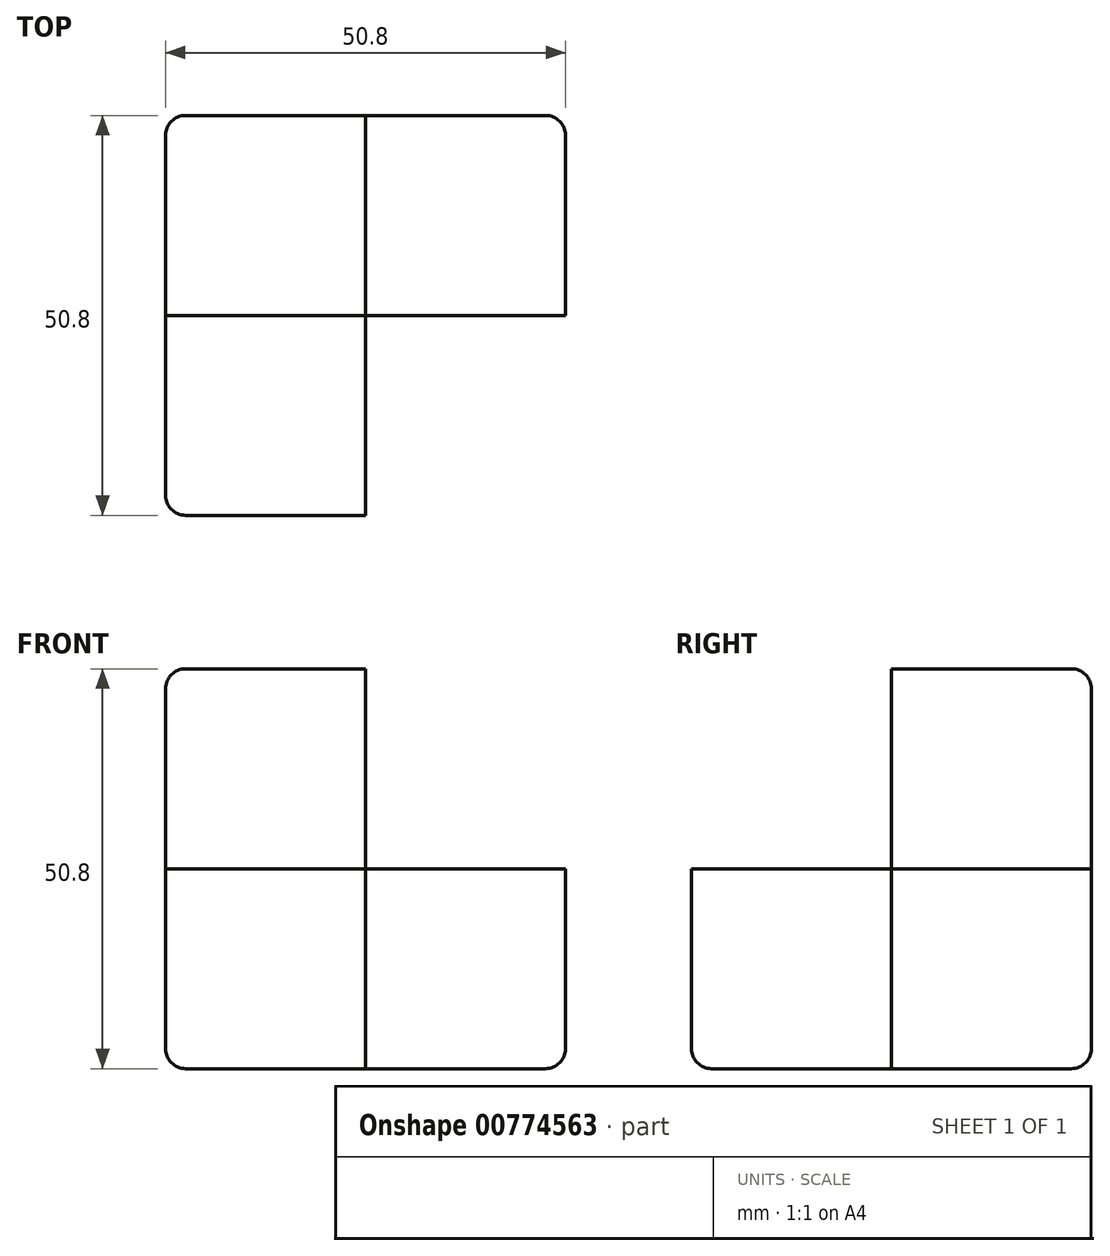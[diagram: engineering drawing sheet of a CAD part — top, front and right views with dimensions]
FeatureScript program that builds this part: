
annotation { "Feature Type Name" : "Feature", "Feature Type Description" : "" }
export const myFeature = defineFeature(function(context is Context, id is Id, definition is map)
    precondition{}
    {
        {
            var Q0;
            Q0=qCreatedBy(makeId("Front.planeOp"),FACE);
            var sketch = newSketch(context, id + "F0", { "sketchPlane" : qUnion([Q0])});
            skLineSegment(sketch, "E0.bottom", {"start": v(0, 0) * mm, "end": v(50.8, 0) * mm});
            skLineSegment(sketch, "E0.top", {"start": v(0, 50.8) * mm, "end": v(50.8, 50.8) * mm});
            skLineSegment(sketch, "E0.left", {"start": v(0, 0) * mm, "end": v(0, 50.8) * mm});
            skLineSegment(sketch, "E0.right", {"start": v(50.8, 0) * mm, "end": v(50.8, 50.8) * mm});
            skSolve(sketch);
        }
        {
            var Q0;
            Q0=makeQuery(id+"F0.imprint","IMPRINT",FACE,{"disambiguationData":[TD([[makeQuery(id+"F0.imprint","IMPRINT",EDGE,{"derivedFrom":sQuery(id+"F0.wireOp",EDGE,"E0.bottom")}),1.0]])]});
            extrude(context, id + "F1", {"entities" : qUnion([Q0]), "depth" : 50.8 * mm, "offsetDistance" : 25.4 * mm});
        }
        {
            var Q0;
            Q0=makeQuery(id+"F1.opExtrude","SWEPT_FACE",FACE,{"disambiguationData":[OSD([sQuery(id+"F0.wireOp",EDGE,"E0.top")])]});
            var sketch = newSketch(context, id + "F2", { "sketchPlane" : qUnion([Q0])});
            skLineSegment(sketch, "E1.bottom", {"start": v(0, 0) * mm, "end": v(25.4, 0) * mm});
            skLineSegment(sketch, "E1.top", {"start": v(0, -25.4) * mm, "end": v(25.4, -25.4) * mm});
            skLineSegment(sketch, "E1.left", {"start": v(0, 0) * mm, "end": v(0, -25.4) * mm});
            skLineSegment(sketch, "E1.right", {"start": v(25.4, 0) * mm, "end": v(25.4, -25.4) * mm});
            skSolve(sketch);
        }
        {
            var Q0;
            {var subQ4=sQuery(id+"F2.wireOp",EDGE,"E1.top");Q0=makeQuery(id+"F2.imprint","IMPRINT",FACE,{"disambiguationData":[TD([[makeQuery(id+"F2.imprint","IMPRINT",EDGE,{"derivedFrom":subQ4}),-1.0]])]});}
            extrude(context, id + "F3", {"entities" : qUnion([Q0]), "operationType" : NewBodyOperationType.REMOVE, "oppositeDirection" : true, "depth" : 25.4 * mm, "offsetDistance" : 25.4 * mm});
        }
        {
            var Q0;
            Q0=makeQuery(id+"F3.boolean.opBoolean","COPY",FACE,{"derivedFrom":makeQuery(id+"F3.opExtrude","CAP_FACE",FACE,{"disambiguationData":[OSD([sQuery(id+"F0.wireOp",EDGE,"E0.top"),sQuery(id+"F0.wireOp",EDGE,"E0.left"),sQuery(id+"F0.wireOp",EDGE,"E0.right"),sQuery(id+"F2.wireOp",EDGE,"E1.top"),sQuery(id+"F2.wireOp",EDGE,"E1.right")])],"isStart":false})});
            var sketch = newSketch(context, id + "F4", { "sketchPlane" : qUnion([Q0])});
            skLineSegment(sketch, "E2.bottom", {"start": v(50.8, -50.8) * mm, "end": v(25.4, -50.8) * mm});
            skLineSegment(sketch, "E2.top", {"start": v(50.8, -25.4) * mm, "end": v(25.4, -25.4) * mm});
            skLineSegment(sketch, "E2.left", {"start": v(50.8, -50.8) * mm, "end": v(50.8, -25.4) * mm});
            skLineSegment(sketch, "E2.right", {"start": v(25.4, -50.8) * mm, "end": v(25.4, -25.4) * mm});
            skSolve(sketch);
        }
        {
            var Q0;
            Q0=makeQuery(id+"F4.imprint","IMPRINT",FACE,{"disambiguationData":[TD([[makeQuery(id+"F4.imprint","IMPRINT",EDGE,{"derivedFrom":sQuery(id+"F4.wireOp",EDGE,"E2.bottom")}),1.0]])]});
            extrude(context, id + "F5", {"entities" : qUnion([Q0]), "operationType" : NewBodyOperationType.REMOVE, "oppositeDirection" : true, "depth" : 25.4 * mm, "offsetDistance" : 25.4 * mm});
        }
        {
            var Q0;
            Q0=makeQuery(id+"F3.boolean.opBoolean","COPY",EDGE,{"derivedFrom":makeQuery(id+"F3.opExtrude","CAP_EDGE",EDGE,{"disambiguationData":[OSD([sQuery(id+"F0.wireOp",EDGE,"E0.top"),sQuery(id+"F0.wireOp",EDGE,"E0.right")])],"isStart":false})});
            var Q1;
            Q1=makeQuery(id+"F3.boolean.opBoolean","COPY",EDGE,{"derivedFrom":makeQuery(id+"F3.opExtrude","CAP_EDGE",EDGE,{"disambiguationData":[OSD([sQuery(id+"F0.wireOp",EDGE,"E0.top"),sQuery(id+"F0.wireOp",EDGE,"E0.left")])],"isStart":false})});
            var Q2;
            Q2=makeQuery(id+"F3.boolean.opBoolean","COPY",EDGE,{"derivedFrom":makeQuery(id+"F3.opExtrude","CAP_EDGE",EDGE,{"disambiguationData":[OSD([sQuery(id+"F2.wireOp",EDGE,"E1.right")])],"isStart":true})});
            var Q3;
            Q3=makeQuery(id+"F3.boolean.opBoolean","COPY",EDGE,{"derivedFrom":makeQuery(id+"F3.opExtrude","CAP_EDGE",EDGE,{"disambiguationData":[OSD([sQuery(id+"F2.wireOp",EDGE,"E1.top")])],"isStart":true})});
            var Q4;
            Q4=makeQuery(id+"F1.opExtrude","SWEPT_EDGE",EDGE,{"disambiguationData":[OSD([sQuery(id+"F0.wireOp",EDGE,"E0.top"),sQuery(id+"F0.wireOp",EDGE,"E0.left")])]});
            var Q5;
            Q5=makeQuery(id+"F1.opExtrude","CAP_EDGE",EDGE,{"disambiguationData":[OSD([sQuery(id+"F0.wireOp",EDGE,"E0.top")])],"isStart":true});
            var Q6;
            {var subQ0=sQuery(id+"F0.wireOp",EDGE,"E0.top");var subQ1=makeQuery(id+"F1.opExtrude","CAP_EDGE",EDGE,{"disambiguationData":[OSD([subQ0])],"isStart":true});Q6=makeQuery(id+"F3.boolean.opBoolean","COPY",EDGE,{"derivedFrom":makeQuery(id+"F3.opExtrude","CAP_EDGE",EDGE,{"disambiguationData":[OSD([subQ0]),TDD([makeQuery(id+"F2.imprint","IMPRINT",EDGE,{"disambiguationData":[TD([[makeQuery(id+"F2.imprint","INTERSECT",VERTEX,{"derivedFrom":[makeQuery(id+"F1.opExtrude","SWEPT_EDGE",EDGE,{"disambiguationData":[OSD([subQ0,sQuery(id+"F0.wireOp",EDGE,"E0.right")])]}),subQ1]}),1.0]])],"derivedFrom":subQ1})])],"isStart":false})});}
            var Q7;
            Q7=makeQuery(id+"F3.boolean.opBoolean","COPY",EDGE,{"derivedFrom":makeQuery(id+"F3.opExtrude","SWEPT_EDGE",EDGE,{"disambiguationData":[OSD([sQuery(id+"F0.wireOp",EDGE,"E0.top"),sQuery(id+"F2.wireOp",EDGE,"E1.bottom"),sQuery(id+"F2.wireOp",EDGE,"E1.right")])]})});
            var Q8;
            {var subQ0=sQuery(id+"F0.wireOp",EDGE,"E0.top");Q8=makeQuery(id+"F3.boolean.opBoolean","COPY",EDGE,{"derivedFrom":makeQuery(id+"F3.opExtrude","CAP_EDGE",EDGE,{"disambiguationData":[OSD([subQ0]),TDD([makeQuery(id+"F2.imprint","IMPRINT",EDGE,{"derivedFrom":makeQuery(id+"F1.opExtrude","CAP_EDGE",EDGE,{"disambiguationData":[OSD([subQ0])],"isStart":false})})])],"isStart":false})});}
            var Q9;
            Q9=makeQuery(id+"F1.opExtrude","CAP_EDGE",EDGE,{"disambiguationData":[OSD([sQuery(id+"F0.wireOp",EDGE,"E0.bottom")])],"isStart":false});
            var Q10;
            Q10=makeQuery(id+"F5.boolean.opBoolean","COPY",EDGE,{"derivedFrom":makeQuery(id+"F5.opExtrude","CAP_EDGE",EDGE,{"disambiguationData":[OSD([sQuery(id+"F4.wireOp",EDGE,"E2.top")])],"isStart":false})});
            var Q11;
            Q11=makeQuery(id+"F5.boolean.opBoolean","COPY",EDGE,{"derivedFrom":makeQuery(id+"F5.opExtrude","SWEPT_EDGE",EDGE,{"disambiguationData":[OSD([sQuery(id+"F0.wireOp",EDGE,"E0.top"),sQuery(id+"F0.wireOp",EDGE,"E0.right"),sQuery(id+"F4.wireOp",EDGE,"E2.top"),sQuery(id+"F4.wireOp",EDGE,"E2.left")])]})});
            var Q12;
            Q12=makeQuery(id+"F5.boolean.opBoolean","COPY",EDGE,{"derivedFrom":makeQuery(id+"F5.opExtrude","SWEPT_EDGE",EDGE,{"disambiguationData":[OSD([sQuery(id+"F0.wireOp",EDGE,"E0.top"),sQuery(id+"F4.wireOp",EDGE,"E2.bottom"),sQuery(id+"F4.wireOp",EDGE,"E2.right")])]})});
            var Q13;
            Q13=makeQuery(id+"F1.opExtrude","CAP_EDGE",EDGE,{"disambiguationData":[OSD([sQuery(id+"F0.wireOp",EDGE,"E0.left")])],"isStart":false});
            var Q14;
            Q14=makeQuery(id+"F1.opExtrude","CAP_EDGE",EDGE,{"disambiguationData":[OSD([sQuery(id+"F0.wireOp",EDGE,"E0.bottom")])],"isStart":true});
            var Q15;
            Q15=makeQuery(id+"F1.opExtrude","SWEPT_EDGE",EDGE,{"disambiguationData":[OSD([sQuery(id+"F0.wireOp",EDGE,"E0.bottom"),sQuery(id+"F0.wireOp",EDGE,"E0.right")])]});
            var Q16;
            Q16=makeQuery(id+"F1.opExtrude","CAP_EDGE",EDGE,{"disambiguationData":[OSD([sQuery(id+"F0.wireOp",EDGE,"E0.left")])],"isStart":true});
            var Q17;
            Q17=makeQuery(id+"F1.opExtrude","SWEPT_EDGE",EDGE,{"disambiguationData":[OSD([sQuery(id+"F0.wireOp",EDGE,"E0.bottom"),sQuery(id+"F0.wireOp",EDGE,"E0.left")])]});
            var Q18;
            Q18=makeQuery(id+"F1.opExtrude","CAP_EDGE",EDGE,{"disambiguationData":[OSD([sQuery(id+"F0.wireOp",EDGE,"E0.right")])],"isStart":true});
            var Q19;
            Q19=makeQuery(id+"F3.boolean.opBoolean","COPY",EDGE,{"derivedFrom":makeQuery(id+"F3.opExtrude","SWEPT_EDGE",EDGE,{"disambiguationData":[OSD([sQuery(id+"F0.wireOp",EDGE,"E0.top"),sQuery(id+"F0.wireOp",EDGE,"E0.left"),sQuery(id+"F2.wireOp",EDGE,"E1.top"),sQuery(id+"F2.wireOp",EDGE,"E1.left")])]})});
            fillet(context, id + "F6", {"entities" : qUnion([Q0, Q1, Q2, Q3, Q4, Q5, Q6, Q7, Q8, Q9, Q10, Q11, Q12, Q13, Q14, Q15, Q16, Q17, Q18, Q19]), "radius" : 2.54 * mm, "tangentPropagation" : true, "allowEdgeOverflow" : false});
        }
    });
